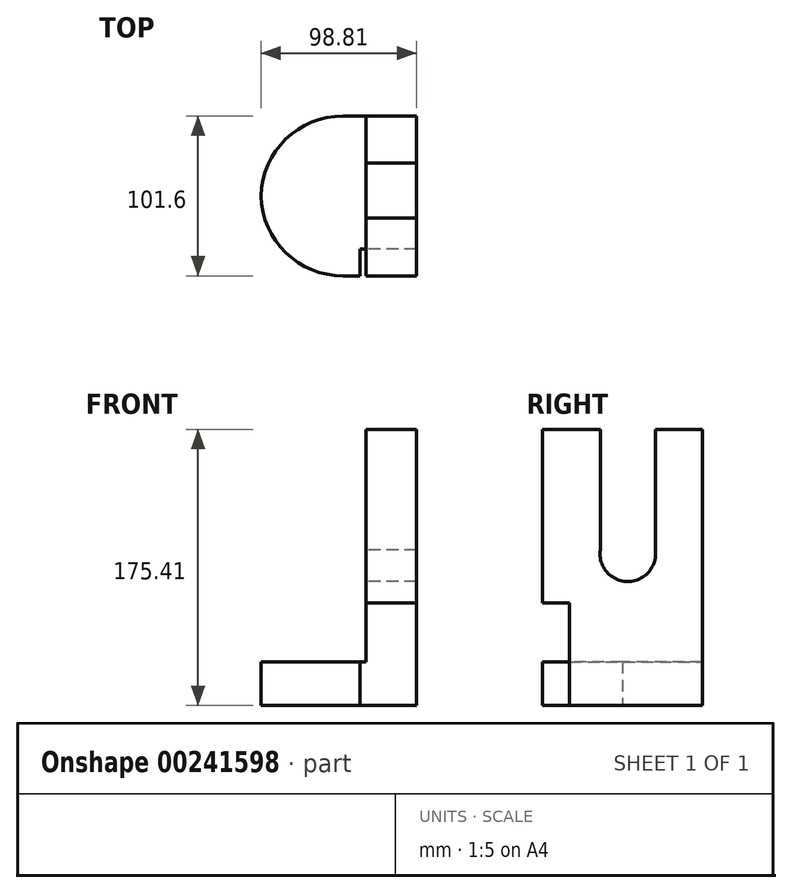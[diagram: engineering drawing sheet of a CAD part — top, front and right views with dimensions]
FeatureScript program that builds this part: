
annotation { "Feature Type Name" : "Feature", "Feature Type Description" : "" }
export const myFeature = defineFeature(function(context is Context, id is Id, definition is map)
    precondition{}
    {
        {
            var Q0;
            Q0=qCreatedBy(makeId("Front.planeOp"),FACE);
            var sketch = newSketch(context, id + "F0", { "sketchPlane" : qUnion([Q0])});
            skLineSegment(sketch, "E0.top", {"start": v(52, -52.17) * mm, "end": v(-46.82, -52.17) * mm});
            skLineSegment(sketch, "E0.left", {"start": v(52, 123.24) * mm, "end": v(52, -52.17) * mm});
            skLineSegment(sketch, "E1.top", {"start": v(-46.82, -24.33) * mm, "end": v(19.86, -24.33) * mm});
            skLineSegment(sketch, "E1.right", {"start": v(19.86, 123.24) * mm, "end": v(19.86, -24.33) * mm});
            skLineSegment(sketch, "E2", {"start": v(-46.82, -24.33) * mm, "end": v(-46.82, -52.17) * mm});
            skLineSegment(sketch, "E3", {"start": v(19.86, 123.24) * mm, "end": v(52, 123.24) * mm});
            skSolve(sketch);
        }
        {
            var Q0;
            Q0 = qSketchRegion(id + "F0", true);
            extrude(context, id + "F1", {"entities" : qUnion([Q0]), "depth" : 101.6 * mm});
        }
        {
            var Q0;
            Q0=makeQuery(id+"F1.opExtrude","CAP_EDGE",EDGE,{"disambiguationData":[OSD([sQuery(id+"F0.wireOp",EDGE,"E2")])],"isStart":true});
            var Q1;
            Q1=makeQuery(id+"F1.opExtrude","CAP_EDGE",EDGE,{"disambiguationData":[OSD([sQuery(id+"F0.wireOp",EDGE,"E2")])],"isStart":false});
            fillet(context, id + "F2", {"entities" : qUnion([Q0, Q1]), "radius" : 52.12 * mm, "tangentPropagation" : true, "allowEdgeOverflow" : false});
        }
        {
            var Q0;
            Q0=qCreatedBy(makeId("Front.planeOp"),FACE);
            var sketch = newSketch(context, id + "F3", { "sketchPlane" : qUnion([Q0])});
            skLineSegment(sketch, "E4.bottom", {"start": v(62.97, 13.14) * mm, "end": v(16.16, 13.14) * mm});
            skLineSegment(sketch, "E4.top", {"start": v(62.97, -65.02) * mm, "end": v(16.16, -65.02) * mm});
            skLineSegment(sketch, "E4.left", {"start": v(62.97, 13.14) * mm, "end": v(62.97, -65.02) * mm});
            skLineSegment(sketch, "E4.right", {"start": v(16.16, 13.14) * mm, "end": v(16.16, -65.02) * mm});
            skSolve(sketch);
        }
        {
            var Q0;
            Q0 = qSketchRegion(id + "F3", true);
            extrude(context, id + "F4", {"entities" : qUnion([Q0]), "operationType" : NewBodyOperationType.REMOVE, "depth" : 123.95 * mm, "hasSecondDirection" : true, "secondDirectionOppositeDirection" : false, "secondDirectionDepth" : 84.58 * mm});
        }
        {
            var Q0;
            Q0=qCreatedBy(makeId("Right.planeOp"),FACE);
            var sketch = newSketch(context, id + "F5", { "sketchPlane" : qUnion([Q0])});
            skLineSegment(sketch, "E5.bottom", {"start": v(-64.93, 125.81) * mm, "end": v(-29.95, 125.81) * mm});
            skLineSegment(sketch, "E5.left", {"start": v(-64.93, 125.81) * mm, "end": v(-64.93, 44.27) * mm});
            skLineSegment(sketch, "E5.right", {"start": v(-29.95, 125.81) * mm, "end": v(-29.95, 44.27) * mm});
            skCircle(sketch, "E6", {"center": v(-47.44, 44.27) * mm, "radius": 17.66 * mm});
            skSolve(sketch);
        }
        {
            var Q0;
            Q0 = qSketchRegion(id + "F5", true);
            extrude(context, id + "F6", {"entities" : qUnion([Q0]), "operationType" : NewBodyOperationType.REMOVE, "endBound" : BoundingType.SYMMETRIC, "depth" : 152.4 * mm});
        }
    });
